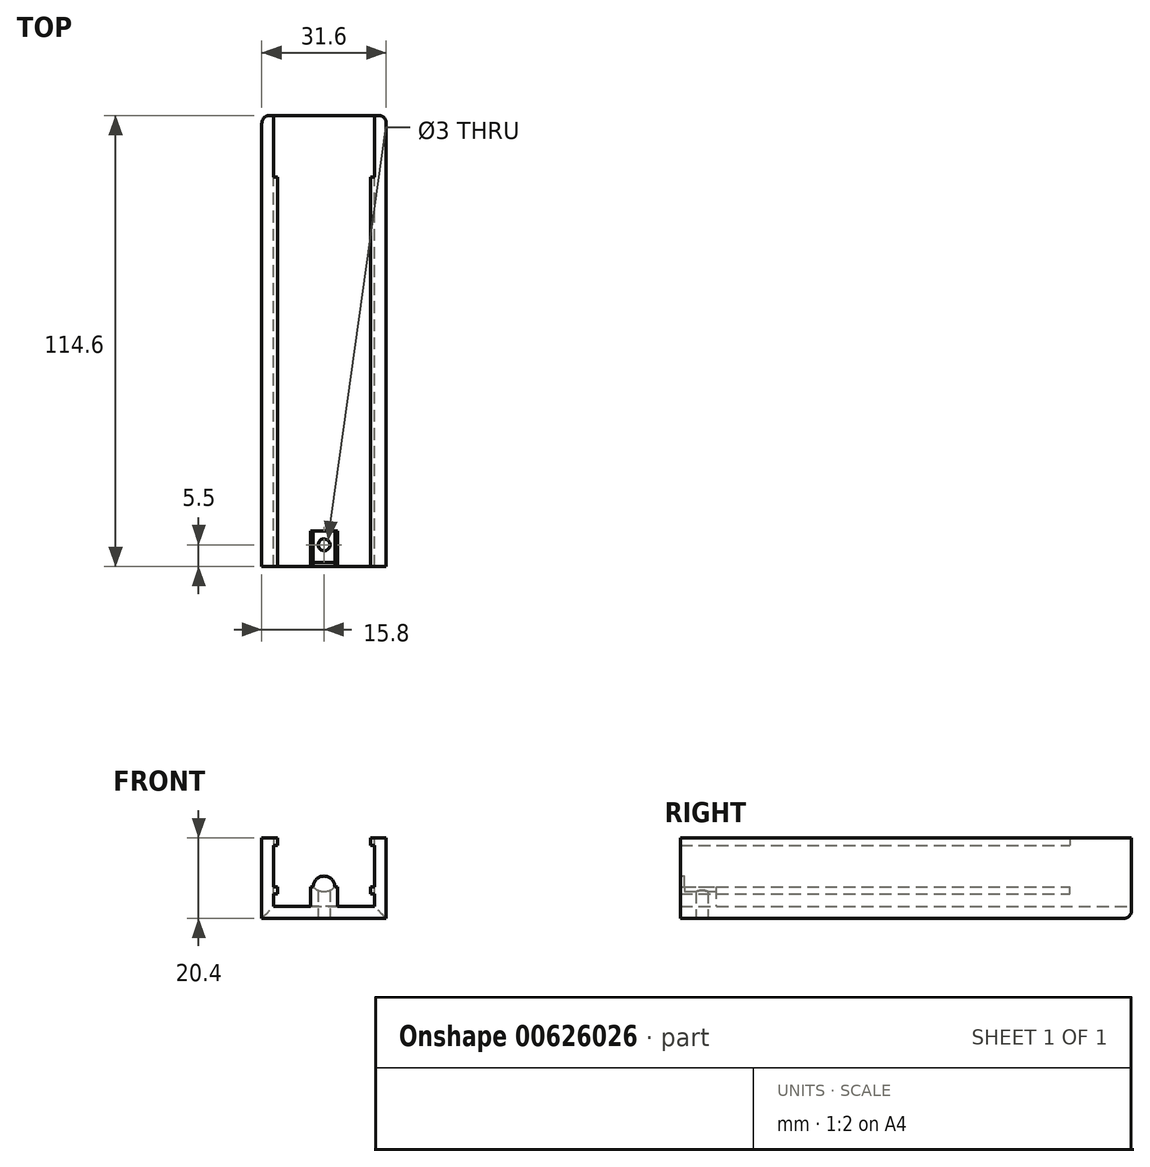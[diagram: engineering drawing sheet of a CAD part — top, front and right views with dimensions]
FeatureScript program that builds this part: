
annotation { "Feature Type Name" : "Feature", "Feature Type Description" : "" }
export const myFeature = defineFeature(function(context is Context, id is Id, definition is map)
    precondition{}
    {
        {
            var Q0;
            Q0=qCreatedBy(makeId("Front.planeOp"),FACE);
            var sketch = newSketch(context, id + "F0", { "sketchPlane" : qUnion([Q0])});
            skLineSegment(sketch, "E0", {"start": v(0, 0) * mm, "end": v(-15.8, 0) * mm});
            skLineSegment(sketch, "E1", {"start": v(-15.8, 0) * mm, "end": v(-15.8, 20.4) * mm});
            skLineSegment(sketch, "E2", {"start": v(-15.8, 20.4) * mm, "end": v(-11.8, 20.4) * mm});
            skLineSegment(sketch, "E3", {"start": v(-11.8, 20.4) * mm, "end": v(-11.8, 18.6) * mm});
            skLineSegment(sketch, "E4", {"start": v(-11.8, 18.6) * mm, "end": v(-12.8, 18.6) * mm});
            skLineSegment(sketch, "E5", {"start": v(3.4, 3) * mm, "end": v(3.4, 8) * mm});
            skLineSegment(sketch, "E6", {"start": v(-3.4, 8) * mm, "end": v(3.4, 8) * mm});
            skLineSegment(sketch, "E7", {"start": v(-3.4, 8) * mm, "end": v(-3.4, 3) * mm});
            skLineSegment(sketch, "E8", {"start": v(12.8, 3) * mm, "end": v(12.8, 6.2) * mm});
            skLineSegment(sketch, "E9", {"start": v(12.8, 6.2) * mm, "end": v(11.8, 6.2) * mm});
            skLineSegment(sketch, "E10", {"start": v(11.8, 6.2) * mm, "end": v(11.8, 8) * mm});
            skLineSegment(sketch, "E11", {"start": v(11.8, 8) * mm, "end": v(12.8, 8) * mm});
            skLineSegment(sketch, "E12", {"start": v(12.8, 8) * mm, "end": v(12.8, 18.6) * mm});
            skLineSegment(sketch, "E13", {"start": v(12.8, 18.6) * mm, "end": v(11.8, 18.6) * mm});
            skLineSegment(sketch, "E14", {"start": v(11.8, 18.6) * mm, "end": v(11.8, 20.4) * mm});
            skLineSegment(sketch, "E15", {"start": v(11.8, 20.4) * mm, "end": v(15.8, 20.4) * mm});
            skLineSegment(sketch, "E16", {"start": v(15.8, 20.4) * mm, "end": v(15.8, 0) * mm});
            skLineSegment(sketch, "E17", {"start": v(15.8, 0) * mm, "end": v(0, 0) * mm});
            skLineSegment(sketch, "E18", {"start": v(-12.8, 3) * mm, "end": v(-12.8, 6.2) * mm});
            skLineSegment(sketch, "E19", {"start": v(-12.8, 6.2) * mm, "end": v(-11.8, 6.2) * mm});
            skLineSegment(sketch, "E20", {"start": v(-11.8, 6.2) * mm, "end": v(-11.8, 8) * mm});
            skLineSegment(sketch, "E21", {"start": v(-11.8, 8) * mm, "end": v(-12.8, 8) * mm});
            skLineSegment(sketch, "E22", {"start": v(-12.8, 8) * mm, "end": v(-12.8, 18.6) * mm});
            skLineSegment(sketch, "E23", {"start": v(-12.8, 3) * mm, "end": v(-3.4, 3) * mm});
            skLineSegment(sketch, "E24", {"start": v(3.4, 3) * mm, "end": v(12.8, 3) * mm});
            skPoint(sketch, "E25.end.orphan", {"position": v(0, 8) * mm});
            skPoint(sketch, "E25.start.orphan", {"position": v(0, 17.14) * mm});
            skLineSegment(sketch, "E26", {"start": v(0, 8) * mm, "end": v(0, 10.75) * mm});
            skArc(sketch, "E27", {"start": v(0, 10.75) * mm, "mid": v(-1.94, 9.94) * mm, "end": v(-2.75, 8) * mm});
            skArc(sketch, "E28", {"start": v(0, 10.75) * mm, "mid": v(1.94, 9.94) * mm, "end": v(2.75, 8) * mm});
            skSolve(sketch);
        }
        {
            var Q0;
            Q0 = qSketchRegion(id + "F0", true);
            extrude(context, id + "F1", {"entities" : qUnion([Q0]), "depth" : 114.6 * mm, "offsetDistance" : 25 * mm});
        }
        {
            var Q0;
            Q0=makeQuery(id+"F1.opExtrude","CAP_FACE",FACE,{"disambiguationData":[OSD([sQuery(id+"F0.wireOp",EDGE,"E0"),sQuery(id+"F0.wireOp",EDGE,"E1"),sQuery(id+"F0.wireOp",EDGE,"E2"),sQuery(id+"F0.wireOp",EDGE,"E3"),sQuery(id+"F0.wireOp",EDGE,"E4"),sQuery(id+"F0.wireOp",EDGE,"E5"),sQuery(id+"F0.wireOp",EDGE,"E6"),sQuery(id+"F0.wireOp",EDGE,"E7"),sQuery(id+"F0.wireOp",EDGE,"E8"),sQuery(id+"F0.wireOp",EDGE,"E9"),sQuery(id+"F0.wireOp",EDGE,"E10"),sQuery(id+"F0.wireOp",EDGE,"E11"),sQuery(id+"F0.wireOp",EDGE,"E12"),sQuery(id+"F0.wireOp",EDGE,"E13"),sQuery(id+"F0.wireOp",EDGE,"E14"),sQuery(id+"F0.wireOp",EDGE,"E15"),sQuery(id+"F0.wireOp",EDGE,"E16"),sQuery(id+"F0.wireOp",EDGE,"E17"),sQuery(id+"F0.wireOp",EDGE,"E18"),sQuery(id+"F0.wireOp",EDGE,"E19"),sQuery(id+"F0.wireOp",EDGE,"E20"),sQuery(id+"F0.wireOp",EDGE,"E21"),sQuery(id+"F0.wireOp",EDGE,"E22"),sQuery(id+"F0.wireOp",EDGE,"E23"),sQuery(id+"F0.wireOp",EDGE,"E24"),sQuery(id+"F0.wireOp",EDGE,"E27"),sQuery(id+"F0.wireOp",EDGE,"E28")])],"isStart":true});
            var sketch = newSketch(context, id + "F2", { "sketchPlane" : qUnion([Q0])});
            skLineSegment(sketch, "E29", {"start": v(-3.4, 3) * mm, "end": v(-3.4, 8) * mm});
            skLineSegment(sketch, "E30", {"start": v(-3.4, 8) * mm, "end": v(-2.75, 8) * mm});
            skLineSegment(sketch, "E31", {"start": v(3.4, 3) * mm, "end": v(3.4, 8) * mm});
            skLineSegment(sketch, "E32", {"start": v(3.4, 8) * mm, "end": v(2.75, 8) * mm});
            skLineSegment(sketch, "E33", {"start": v(-3.4, 3) * mm, "end": v(3.4, 3) * mm});
            skArc(sketch, "E34", {"start": v(-2.75, 8) * mm, "mid": v(0, 10.75) * mm, "end": v(2.75, 8) * mm});
            skSolve(sketch);
        }
        {
            var Q0;
            Q0 = qSketchRegion(id + "F2", true);
            extrude(context, id + "F3", {"entities" : qUnion([Q0]), "operationType" : NewBodyOperationType.REMOVE, "oppositeDirection" : true, "depth" : 105.6 * mm, "offsetDistance" : 25 * mm});
        }
        {
            var Q0;
            Q0=makeQuery(id+"F3.boolean.opBoolean","COPY",FACE,{"derivedFrom":makeQuery(id+"F3.opExtrude","CAP_FACE",FACE,{"disambiguationData":[OSD([sQuery(id+"F2.wireOp",EDGE,"E29"),sQuery(id+"F2.wireOp",EDGE,"E30"),sQuery(id+"F2.wireOp",EDGE,"E31"),sQuery(id+"F2.wireOp",EDGE,"E32"),sQuery(id+"F2.wireOp",EDGE,"E33"),sQuery(id+"F2.wireOp",EDGE,"E34")])],"isStart":false})});
            var sketch = newSketch(context, id + "F4", { "sketchPlane" : qUnion([Q0])});
            skArc(sketch, "E35", {"start": v(-2.75, 8) * mm, "mid": v(0, 6.83) * mm, "end": v(2.75, 8) * mm});
            skArc(sketch, "E36", {"start": v(-2.75, 8) * mm, "mid": v(0, 10.75) * mm, "end": v(2.75, 8) * mm});
            skLineSegment(sketch, "E37", {"start": v(0, 3) * mm, "end": v(0, 7.45) * mm});
            skSolve(sketch);
        }
        {
            var Q0;
            Q0 = qSketchRegion(id + "F4", true);
            extrude(context, id + "F5", {"entities" : qUnion([Q0]), "operationType" : NewBodyOperationType.REMOVE, "oppositeDirection" : true, "depth" : 8 * mm, "offsetDistance" : 25 * mm});
        }
        {
            var Q0;
            Q0=makeQuery(id+"F1.opExtrude","SWEPT_FACE",FACE,{"disambiguationData":[OSD([sQuery(id+"F0.wireOp",EDGE,"E0"),sQuery(id+"F0.wireOp",EDGE,"E17")])]});
            var sketch = newSketch(context, id + "F6", { "sketchPlane" : qUnion([Q0])});
            skCircle(sketch, "E38", {"center": v(0, 109.1) * mm, "radius": 1.5 * mm});
            skPoint(sketch, "E38.centerSnap0", {"position": v(0, 114.6) * mm});
            skSolve(sketch);
        }
        {
            var Q0;
            Q0 = qSketchRegion(id + "F6", true);
            extrude(context, id + "F7", {"entities" : qUnion([Q0]), "operationType" : NewBodyOperationType.REMOVE, "endBound" : BoundingType.THROUGH_ALL, "oppositeDirection" : true, "depth" : 25 * mm, "offsetDistance" : 25 * mm});
        }
        {
            var Q0;
            Q0=makeQuery(id+"F1.opExtrude","CAP_FACE",FACE,{"disambiguationData":[OSD([sQuery(id+"F0.wireOp",EDGE,"E0"),sQuery(id+"F0.wireOp",EDGE,"E1"),sQuery(id+"F0.wireOp",EDGE,"E2"),sQuery(id+"F0.wireOp",EDGE,"E3"),sQuery(id+"F0.wireOp",EDGE,"E4"),sQuery(id+"F0.wireOp",EDGE,"E5"),sQuery(id+"F0.wireOp",EDGE,"E6"),sQuery(id+"F0.wireOp",EDGE,"E7"),sQuery(id+"F0.wireOp",EDGE,"E8"),sQuery(id+"F0.wireOp",EDGE,"E9"),sQuery(id+"F0.wireOp",EDGE,"E10"),sQuery(id+"F0.wireOp",EDGE,"E11"),sQuery(id+"F0.wireOp",EDGE,"E12"),sQuery(id+"F0.wireOp",EDGE,"E13"),sQuery(id+"F0.wireOp",EDGE,"E14"),sQuery(id+"F0.wireOp",EDGE,"E15"),sQuery(id+"F0.wireOp",EDGE,"E16"),sQuery(id+"F0.wireOp",EDGE,"E17"),sQuery(id+"F0.wireOp",EDGE,"E18"),sQuery(id+"F0.wireOp",EDGE,"E19"),sQuery(id+"F0.wireOp",EDGE,"E20"),sQuery(id+"F0.wireOp",EDGE,"E21"),sQuery(id+"F0.wireOp",EDGE,"E22"),sQuery(id+"F0.wireOp",EDGE,"E23"),sQuery(id+"F0.wireOp",EDGE,"E24"),sQuery(id+"F0.wireOp",EDGE,"E27"),sQuery(id+"F0.wireOp",EDGE,"E28")])],"isStart":true});
            var sketch = newSketch(context, id + "F8", { "sketchPlane" : qUnion([Q0])});
            skLineSegment(sketch, "E39", {"start": v(-11.8, 18.6) * mm, "end": v(-12.8, 18.6) * mm});
            skLineSegment(sketch, "E40", {"start": v(-12.8, 18.6) * mm, "end": v(-12.8, 20.4) * mm});
            skLineSegment(sketch, "E41", {"start": v(-12.8, 20.4) * mm, "end": v(-11.8, 20.4) * mm});
            skLineSegment(sketch, "E42", {"start": v(-11.8, 20.4) * mm, "end": v(-11.8, 18.6) * mm});
            skLineSegment(sketch, "E43", {"start": v(-11.8, 8) * mm, "end": v(-11.8, 6.2) * mm});
            skLineSegment(sketch, "E44", {"start": v(-11.8, 6.2) * mm, "end": v(-12.8, 6.2) * mm});
            skLineSegment(sketch, "E45", {"start": v(-12.8, 6.2) * mm, "end": v(-12.8, 8) * mm});
            skLineSegment(sketch, "E46", {"start": v(-12.8, 8) * mm, "end": v(-11.8, 8) * mm});
            skLineSegment(sketch, "E47", {"start": v(11.8, 8) * mm, "end": v(11.8, 6.2) * mm});
            skLineSegment(sketch, "E48", {"start": v(11.8, 6.2) * mm, "end": v(12.8, 6.2) * mm});
            skLineSegment(sketch, "E49", {"start": v(12.8, 6.2) * mm, "end": v(12.8, 8) * mm});
            skLineSegment(sketch, "E50", {"start": v(12.8, 8) * mm, "end": v(11.8, 8) * mm});
            skLineSegment(sketch, "E51", {"start": v(12.8, 18.6) * mm, "end": v(11.8, 18.6) * mm});
            skLineSegment(sketch, "E52", {"start": v(11.8, 18.6) * mm, "end": v(11.8, 20.4) * mm});
            skLineSegment(sketch, "E53", {"start": v(11.8, 20.4) * mm, "end": v(12.8, 20.4) * mm});
            skPoint(sketch, "E53.endSnap0", {"position": v(12.8, 13.3) * mm});
            skLineSegment(sketch, "E54", {"start": v(12.8, 20.4) * mm, "end": v(12.8, 18.6) * mm});
            skSolve(sketch);
        }
        {
            var Q0;
            Q0 = qSketchRegion(id + "F8", true);
            extrude(context, id + "F9", {"entities" : qUnion([Q0]), "operationType" : NewBodyOperationType.REMOVE, "oppositeDirection" : true, "depth" : 15.6 * mm, "offsetDistance" : 25 * mm});
        }
        {
            var Q0;
            Q0=makeQuery(id+"F9.boolean.opBoolean","MERGE",EDGE,{"derivedFrom":[makeQuery(id+"F1.opExtrude","CAP_EDGE",EDGE,{"disambiguationData":[OSD([sQuery(id+"F0.wireOp",EDGE,"E8")])],"isStart":true}),makeQuery(id+"F1.opExtrude","CAP_EDGE",EDGE,{"disambiguationData":[OSD([sQuery(id+"F0.wireOp",EDGE,"E12")])],"isStart":true}),makeQuery(id+"F9.opExtrude","CAP_EDGE",EDGE,{"disambiguationData":[OSD([sQuery(id+"F8.wireOp",EDGE,"E40")])],"isStart":true}),makeQuery(id+"F9.opExtrude","CAP_EDGE",EDGE,{"disambiguationData":[OSD([sQuery(id+"F8.wireOp",EDGE,"E45")])],"isStart":true})]});
            var Q1;
            Q1=makeQuery(id+"F1.opExtrude","CAP_EDGE",EDGE,{"disambiguationData":[OSD([sQuery(id+"F0.wireOp",EDGE,"E16")])],"isStart":true});
            var Q2;
            Q2=makeQuery(id+"F3.boolean.opBoolean","MERGE",EDGE,{"derivedFrom":[makeQuery(id+"F1.opExtrude","CAP_EDGE",EDGE,{"disambiguationData":[OSD([sQuery(id+"F0.wireOp",EDGE,"E23")])],"isStart":true}),makeQuery(id+"F1.opExtrude","CAP_EDGE",EDGE,{"disambiguationData":[OSD([sQuery(id+"F0.wireOp",EDGE,"E24")])],"isStart":true}),makeQuery(id+"F3.opExtrude","CAP_EDGE",EDGE,{"disambiguationData":[OSD([sQuery(id+"F2.wireOp",EDGE,"E33")])],"isStart":true})]});
            var Q3;
            Q3=makeQuery(id+"F1.opExtrude","CAP_EDGE",EDGE,{"disambiguationData":[OSD([sQuery(id+"F0.wireOp",EDGE,"E0"),sQuery(id+"F0.wireOp",EDGE,"E17")])],"isStart":true});
            var Q4;
            Q4=makeQuery(id+"F1.opExtrude","CAP_EDGE",EDGE,{"disambiguationData":[OSD([sQuery(id+"F0.wireOp",EDGE,"E1")])],"isStart":true});
            var Q5;
            Q5=makeQuery(id+"F9.boolean.opBoolean","MERGE",EDGE,{"derivedFrom":[makeQuery(id+"F1.opExtrude","CAP_EDGE",EDGE,{"disambiguationData":[OSD([sQuery(id+"F0.wireOp",EDGE,"E18")])],"isStart":true}),makeQuery(id+"F1.opExtrude","CAP_EDGE",EDGE,{"disambiguationData":[OSD([sQuery(id+"F0.wireOp",EDGE,"E22")])],"isStart":true}),makeQuery(id+"F9.opExtrude","CAP_EDGE",EDGE,{"disambiguationData":[OSD([sQuery(id+"F8.wireOp",EDGE,"E49")])],"isStart":true}),makeQuery(id+"F9.opExtrude","CAP_EDGE",EDGE,{"disambiguationData":[OSD([sQuery(id+"F8.wireOp",EDGE,"E54")])],"isStart":true})]});
            fillet(context, id + "F10", {"entities" : qUnion([Q0, Q1, Q2, Q3, Q4, Q5]), "radius" : 2 * mm, "tangentPropagation" : true, "allowEdgeOverflow" : false});
        }
    });
